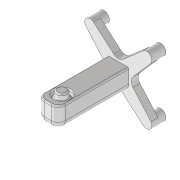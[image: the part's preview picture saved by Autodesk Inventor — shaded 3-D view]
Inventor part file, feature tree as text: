
AUTODESK INVENTOR PART (.ipt)
format: ipt  version: 2020 (Build 240168000, 168)  size: 203,264 bytes
history: native  units: mm
features: extrude x5, sketch x5, fillet x4, chamfer x1
ambient origin geometry x8: Origin, YZ Plane, XZ Plane, XY Plane, X Axis, Y Axis, Z Axis, Center Point
bodies: Volumenkörper1 (feature_tree)
feature tree (15):
  extrude  "Extrusion1"  Depth=30.0mm
  extrude  "Extrusion2"  Depth=15.0mm
  extrude  "Extrusion3"  Depth=15.0mm
  extrude  "Extrusion4"  Depth=15.0mm
  extrude  "Extrusion5"  Depth=10.0mm TaperAngle=0.0deg
  fillet  "Rundung1"  Radius=10.0mm
  fillet  "Rundung2"  Radius=25.0mm
  chamfer  "Fase3"  Distance=20.0mm
  fillet  "Rundung3"  Radius=5.0mm
  fillet  "Rundung4"  Radius=15.0mm
  sketch  "Skizze1"  dims[d0=30.0mm d1=30.0mm]
  sketch  "Skizze2"  dims[d2=100.0mm d3=0.0mm d4=15.0mm]
  sketch  "Skizze3"  dims[d5=15.0mm d6=15.0mm]
  sketch  "Skizze4"  dims[d7=15.0mm d8=40.0mm]
  sketch  "Skizze5"  dims[d9=40.0mm d10=10.0mm d11=0.0mm d12=10.0mm d13=0.0mm d14=25.0mm d15=20.0mm d16=5.0mm d17=0.0mm d18=15.0mm d19=10.0mm d20=0.0mm d27=10.0mm d28=10.0mm d29=2.0mm d30=2.0mm d31=45.0deg d32=2.0mm d33=10.0mm]
